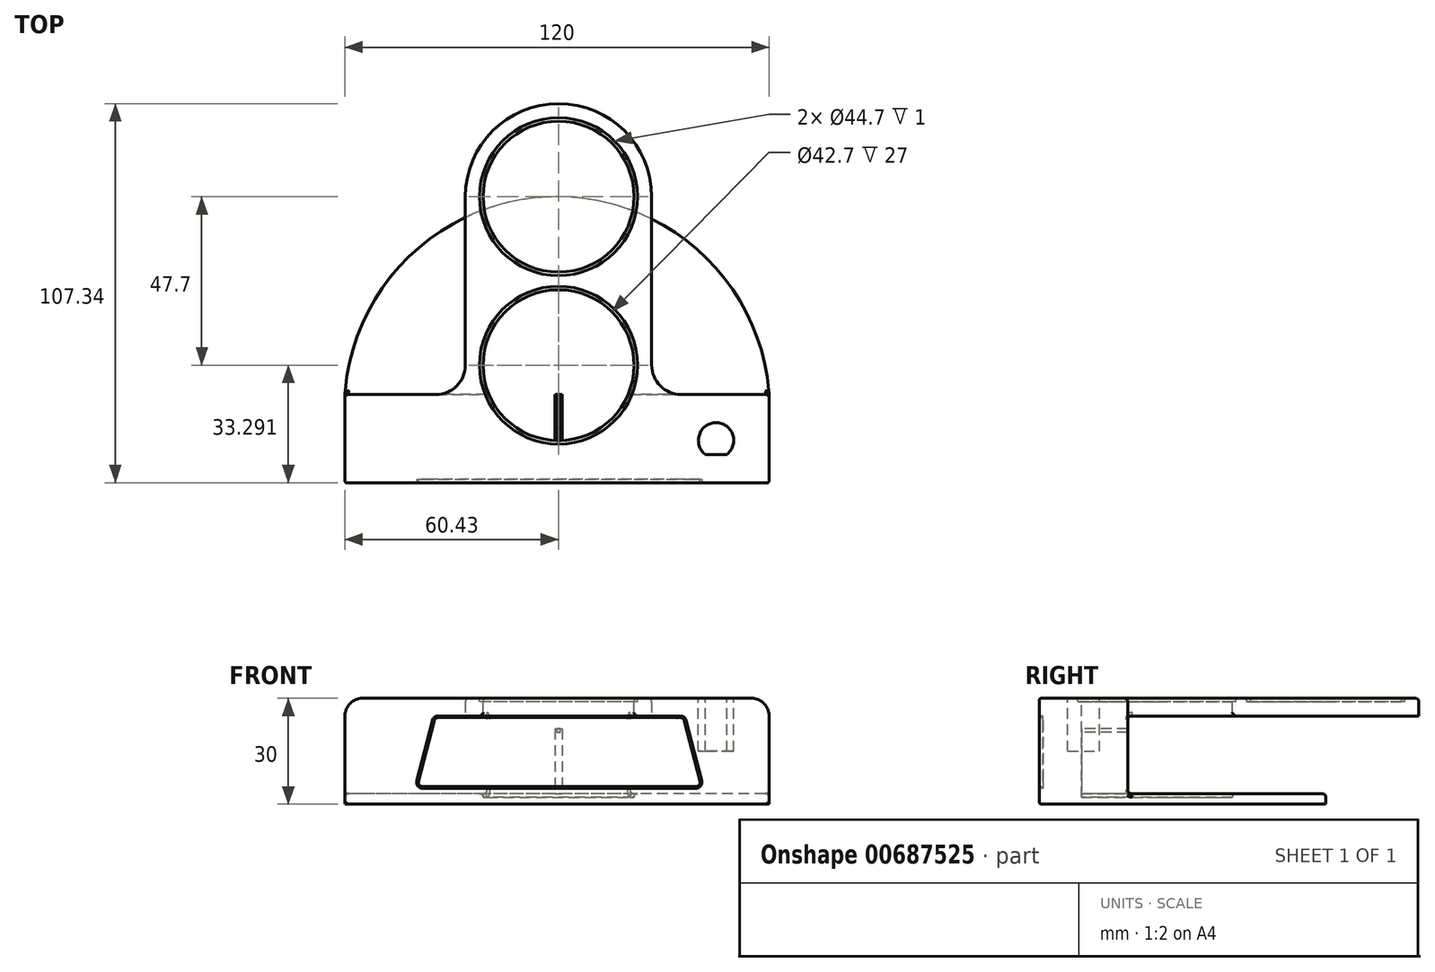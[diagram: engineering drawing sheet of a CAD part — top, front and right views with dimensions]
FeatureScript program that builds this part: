
annotation { "Feature Type Name" : "Feature", "Feature Type Description" : "" }
export const myFeature = defineFeature(function(context is Context, id is Id, definition is map)
    precondition{}
    {
        {
            var Q0;
            Q0=qCreatedBy(makeId("Top.planeOp"),FACE);
            var sketch = newSketch(context, id + "F0", { "sketchPlane" : qUnion([Q0])});
            skLineSegment(sketch, "E0", {"start": v(0, 0) * mm, "end": v(-60.43, 0) * mm, "construction": true});
            skLineSegment(sketch, "E1.bottom", {"start": v(-60.43, 0) * mm, "end": v(59.57, 0) * mm});
            skLineSegment(sketch, "E1.top", {"start": v(-60.43, 25) * mm, "end": v(59.57, 25) * mm});
            skLineSegment(sketch, "E1.left", {"start": v(-60.43, 0) * mm, "end": v(-60.43, 25) * mm});
            skLineSegment(sketch, "E1.right", {"start": v(59.57, 0) * mm, "end": v(59.57, 25) * mm});
            skSolve(sketch);
        }
        {
            var Q0;
            Q0=makeQuery(id+"F0.imprint","IMPRINT",FACE,{"disambiguationData":[TD([[makeQuery(id+"F0.imprint","IMPRINT",EDGE,{"derivedFrom":sQuery(id+"F0.wireOp",EDGE,"E1.bottom")}),1.0]])]});
            extrude(context, id + "F1", {"entities" : qUnion([Q0]), "depth" : 30 * mm, "offsetDistance" : 25 * mm});
        }
        {
            var Q0;
            Q0=qCreatedBy(makeId("Top.planeOp"),FACE);
            cPlane(context, id + "F2", {"entities" : qUnion([Q0]), "cplaneType" : CPlaneType.OFFSET, "offset" : 25 * mm, "width" : 150 * mm, "height" : 150 * mm});
        }
        {
            var Q0;
            Q0=qCreatedBy(id+"F2.planeOp",FACE);
            var sketch = newSketch(context, id + "F3", { "sketchPlane" : qUnion([Q0])});
            skCircle(sketch, "E2", {"center": v(0, 33.3) * mm, "radius": 21.35 * mm});
            skCircle(sketch, "E3", {"center": v(0, 81) * mm, "radius": 21.35 * mm});
            skLineSegment(sketch, "E4.0", {"start": v(-60.43, 25) * mm, "end": v(59.57, 25) * mm});
            skLineSegment(sketch, "E5.0.0", {"start": v(59.57, 25) * mm, "end": v(-60.43, 25) * mm});
            skLineSegment(sketch, "E5.0.1", {"start": v(-60.43, 25) * mm, "end": v(-60.43, 0) * mm});
            skLineSegment(sketch, "E5.0.2", {"start": v(-60.43, 0) * mm, "end": v(59.57, 0) * mm});
            skLineSegment(sketch, "E5.0.3", {"start": v(59.57, 0) * mm, "end": v(59.57, 25) * mm});
            skArc(sketch, "E6", {"start": v(-34.64, 25) * mm, "mid": v(-28.78, 27.43) * mm, "end": v(-26.35, 33.3) * mm});
            skArc(sketch, "E7.0", {"start": v(26.35, 81) * mm, "mid": v(0, 107.34) * mm, "end": v(-26.35, 81) * mm});
            skLineSegment(sketch, "E8", {"start": v(-26.35, 81) * mm, "end": v(-26.35, 33.3) * mm});
            skLineSegment(sketch, "E9", {"start": v(26.35, 81) * mm, "end": v(26.35, 33.3) * mm});
            skArc(sketch, "E10.MirrorC", {"start": v(34.64, 25) * mm, "mid": v(28.78, 27.43) * mm, "end": v(26.35, 33.3) * mm});
            skSolve(sketch);
        }
        {
            var Q0;
            Q0=makeQuery(id+"F3.imprint","IMPRINT",FACE,{"disambiguationData":[TD([[makeQuery(id+"F3.imprint","IMPRINT",EDGE,{"derivedFrom":sQuery(id+"F3.wireOp",EDGE,"E3")}),-1.0]])]});
            var Q1;
            {var subQ0=sQuery(id+"F3.wireOp",EDGE,"E5.0.0");var subQ1=sQuery(id+"F3.wireOp",EDGE,"E2");var subQ2=makeQuery(id+"F3.imprint","INTERSECT",VERTEX,{"disambiguationData":[OD(0.0)],"derivedFrom":[subQ1,subQ0]});Q1=makeQuery(id+"F3.imprint","IMPRINT",FACE,{"disambiguationData":[TD([[makeQuery(id+"F3.imprint","IMPRINT",EDGE,{"disambiguationData":[TD([[subQ2,-1.0]])],"derivedFrom":subQ1}),1.0]])]});}
            var Q2;
            Q2=makeQuery(id+"F3.imprint","IMPRINT",FACE,{"disambiguationData":[TD([[makeQuery(id+"F3.imprint","IMPRINT",EDGE,{"derivedFrom":sQuery(id+"F3.wireOp",EDGE,"E3")}),1.0]])]});
            extrude(context, id + "F4", {"entities" : qUnion([Q0, Q1, Q2]), "operationType" : NewBodyOperationType.ADD, "depth" : 5 * mm, "offsetDistance" : 25 * mm});
        }
        {
            var Q0;
            Q0=qCreatedBy(makeId("Top.planeOp"),FACE);
            var sketch = newSketch(context, id + "F5", { "sketchPlane" : qUnion([Q0])});
            skLineSegment(sketch, "E11.0", {"start": v(59.57, 25) * mm, "end": v(-60.43, 25) * mm});
            skPoint(sketch, "E12.0", {"position": v(0, 81) * mm});
            skArc(sketch, "E13", {"start": v(59.57, 25) * mm, "mid": v(-0.43, 81) * mm, "end": v(-60.43, 25) * mm});
            skLineSegment(sketch, "E14", {"start": v(-60.43, 25) * mm, "end": v(59.57, 25) * mm});
            skSolve(sketch);
        }
        {
            var Q0;
            Q0=makeQuery(id+"F5.imprint","IMPRINT",FACE,{"disambiguationData":[TD([[makeQuery(id+"F5.imprint","IMPRINT",EDGE,{"derivedFrom":sQuery(id+"F5.wireOp",EDGE,"E13")}),1.0]])]});
            extrude(context, id + "F6", {"entities" : qUnion([Q0]), "operationType" : NewBodyOperationType.ADD, "depth" : 3 * mm, "offsetDistance" : 25 * mm});
        }
        {
            var Q0;
            Q0=makeQuery(id+"F6.opExtrude","CAP_EDGE",EDGE,{"disambiguationData":[OSD([sQuery(id+"F5.wireOp",EDGE,"E13")])],"isStart":false});
            var Q1;
            Q1=makeQuery(id+"F1.opExtrude","SWEPT_FACE",FACE,{"disambiguationData":[OSD([sQuery(id+"F0.wireOp",EDGE,"E1.top")])]});
            fillet(context, id + "F7", {"entities" : qUnion([Q0, Q1]), "radius" : 1 * mm, "tangentPropagation" : true, "allowEdgeOverflow" : false});
        }
        {
            var Q0;
            Q0=makeQuery(id+"F4.boolean.opBoolean","MERGE",FACE,{"derivedFrom":[makeQuery(id+"F1.opExtrude","CAP_FACE",FACE,{"disambiguationData":[OSD([sQuery(id+"F0.wireOp",EDGE,"E1.bottom"),sQuery(id+"F0.wireOp",EDGE,"E1.top"),sQuery(id+"F0.wireOp",EDGE,"E1.left"),sQuery(id+"F0.wireOp",EDGE,"E1.right")])],"isStart":false}),makeQuery(id+"F4.opExtrude","CAP_FACE",FACE,{"disambiguationData":[OSD([sQuery(id+"F3.wireOp",EDGE,"E5.0.0"),sQuery(id+"F3.wireOp",EDGE,"E6"),sQuery(id+"F3.wireOp",EDGE,"E7.0"),sQuery(id+"F3.wireOp",EDGE,"E8"),sQuery(id+"F3.wireOp",EDGE,"E9"),sQuery(id+"F3.wireOp",EDGE,"E10.MirrorC")])],"isStart":false})]});
            var sketch = newSketch(context, id + "F8", { "sketchPlane" : qUnion([Q0])});
            skCircle(sketch, "E15.0", {"center": v(0, 81) * mm, "radius": 21.35 * mm});
            skCircle(sketch, "E16.0", {"center": v(0, 33.3) * mm, "radius": 21.35 * mm});
            skCircle(sketch, "E17.0", {"center": v(0, 81) * mm, "radius": 22.35 * mm});
            skCircle(sketch, "E18.0", {"center": v(0, 33.3) * mm, "radius": 22.35 * mm});
            skSolve(sketch);
        }
        {
            var Q0;
            Q0=makeQuery(id+"F8.imprint","IMPRINT",FACE,{"disambiguationData":[TD([[makeQuery(id+"F8.imprint","IMPRINT",EDGE,{"derivedFrom":sQuery(id+"F8.wireOp",EDGE,"E15.0")}),-1.0]])]});
            var Q1;
            Q1=makeQuery(id+"F8.imprint","IMPRINT",FACE,{"disambiguationData":[TD([[makeQuery(id+"F8.imprint","IMPRINT",EDGE,{"derivedFrom":sQuery(id+"F8.wireOp",EDGE,"E16.0")}),-1.0]])]});
            extrude(context, id + "F9", {"entities" : qUnion([Q0, Q1]), "operationType" : NewBodyOperationType.REMOVE, "oppositeDirection" : true, "depth" : 1 * mm, "offsetDistance" : 25 * mm});
        }
        {
            var Q0;
            Q0=makeQuery(id+"F9.boolean.opBoolean","SPLIT",FACE,{"disambiguationData":[TD([makeQuery(id+"F9.opExtrude","SWEPT_FACE",FACE,{"disambiguationData":[OSD([sQuery(id+"F8.wireOp",EDGE,"E15.0")])]})])],"derivedFrom":makeQuery(id+"F4.boolean.opBoolean","MERGE",FACE,{"derivedFrom":[makeQuery(id+"F1.opExtrude","CAP_FACE",FACE,{"disambiguationData":[OSD([sQuery(id+"F0.wireOp",EDGE,"E1.bottom"),sQuery(id+"F0.wireOp",EDGE,"E1.top"),sQuery(id+"F0.wireOp",EDGE,"E1.left"),sQuery(id+"F0.wireOp",EDGE,"E1.right")])],"isStart":false}),makeQuery(id+"F4.opExtrude","CAP_FACE",FACE,{"disambiguationData":[OSD([sQuery(id+"F3.wireOp",EDGE,"E5.0.0"),sQuery(id+"F3.wireOp",EDGE,"E6"),sQuery(id+"F3.wireOp",EDGE,"E7.0"),sQuery(id+"F3.wireOp",EDGE,"E8"),sQuery(id+"F3.wireOp",EDGE,"E9"),sQuery(id+"F3.wireOp",EDGE,"E10.MirrorC")])],"isStart":false})]})});
            extrude(context, id + "F10", {"entities" : qUnion([Q0]), "operationType" : NewBodyOperationType.REMOVE, "oppositeDirection" : true, "depth" : 1 * mm, "offsetDistance" : 25 * mm});
        }
        {
            var Q0;
            Q0=makeQuery(id+"F10.boolean.opBoolean","MERGE",FACE,{"derivedFrom":[makeQuery(id+"F9.boolean.opBoolean","COPY",FACE,{"derivedFrom":makeQuery(id+"F9.opExtrude","CAP_FACE",FACE,{"disambiguationData":[OSD([sQuery(id+"F8.wireOp",EDGE,"E15.0"),sQuery(id+"F8.wireOp",EDGE,"E17.0")])],"isStart":false})}),makeQuery(id+"F10.opExtrude","CAP_FACE",FACE,{"disambiguationData":[OSD([sQuery(id+"F0.wireOp",EDGE,"E1.bottom"),sQuery(id+"F0.wireOp",EDGE,"E1.top"),sQuery(id+"F0.wireOp",EDGE,"E1.left"),sQuery(id+"F0.wireOp",EDGE,"E1.right"),sQuery(id+"F3.wireOp",EDGE,"E5.0.0"),sQuery(id+"F3.wireOp",EDGE,"E6"),sQuery(id+"F3.wireOp",EDGE,"E7.0"),sQuery(id+"F3.wireOp",EDGE,"E8"),sQuery(id+"F3.wireOp",EDGE,"E9"),sQuery(id+"F3.wireOp",EDGE,"E10.MirrorC")])],"isStart":false})]});
            var sketch = newSketch(context, id + "F11", { "sketchPlane" : qUnion([Q0])});
            skCircle(sketch, "E19.0", {"center": v(0, 81) * mm, "radius": 21.35 * mm});
            skSolve(sketch);
        }
        {
            var Q0;
            Q0=makeQuery(id+"F11.imprint","IMPRINT",FACE,{"disambiguationData":[TD([[makeQuery(id+"F11.imprint","IMPRINT",EDGE,{"derivedFrom":sQuery(id+"F11.wireOp",EDGE,"E19.0")}),1.0]])]});
            extrude(context, id + "F12", {"entities" : qUnion([Q0]), "depth" : 1 * mm, "offsetDistance" : 25 * mm});
        }
        {
            var Q0;
            Q0=makeQuery(id+"F9.boolean.opBoolean","SPLIT",FACE,{"disambiguationData":[TD([makeQuery(id+"F9.opExtrude","SWEPT_FACE",FACE,{"disambiguationData":[OSD([sQuery(id+"F8.wireOp",EDGE,"E16.0")])]})])],"derivedFrom":makeQuery(id+"F4.boolean.opBoolean","MERGE",FACE,{"derivedFrom":[makeQuery(id+"F1.opExtrude","CAP_FACE",FACE,{"disambiguationData":[OSD([sQuery(id+"F0.wireOp",EDGE,"E1.bottom"),sQuery(id+"F0.wireOp",EDGE,"E1.top"),sQuery(id+"F0.wireOp",EDGE,"E1.left"),sQuery(id+"F0.wireOp",EDGE,"E1.right")])],"isStart":false}),makeQuery(id+"F4.opExtrude","CAP_FACE",FACE,{"disambiguationData":[OSD([sQuery(id+"F3.wireOp",EDGE,"E5.0.0"),sQuery(id+"F3.wireOp",EDGE,"E6"),sQuery(id+"F3.wireOp",EDGE,"E7.0"),sQuery(id+"F3.wireOp",EDGE,"E8"),sQuery(id+"F3.wireOp",EDGE,"E9"),sQuery(id+"F3.wireOp",EDGE,"E10.MirrorC")])],"isStart":false})]})});
            var Q1;
            Q1=makeQuery(id+"F6.opExtrude","CAP_FACE",FACE,{"disambiguationData":[OSD([sQuery(id+"F5.wireOp",EDGE,"E13"),sQuery(id+"F5.wireOp",EDGE,"E14")])],"isStart":false});
            extrude(context, id + "F13", {"entities" : qUnion([Q0]), "operationType" : NewBodyOperationType.REMOVE, "endBound" : BoundingType.UP_TO_SURFACE, "oppositeDirection" : true, "depth" : 25 * mm, "endBoundEntityFace" : qUnion([Q1]), "offsetDistance" : 25 * mm});
        }
        {
            var Q0;
            {var subQ0=sQuery(id+"F5.wireOp",EDGE,"E14");var subQ1=sQuery(id+"F5.wireOp",EDGE,"E13");Q0=makeQuery(id+"F13.boolean.opBoolean","MERGE",FACE,{"derivedFrom":[makeQuery(id+"F6.opExtrude","CAP_FACE",FACE,{"disambiguationData":[OSD([subQ1,subQ0])],"isStart":false}),makeQuery(id+"F13.opExtrude","CAP_FACE",FACE,{"disambiguationData":[OSD([subQ1,subQ0])],"isStart":false})]});}
            var sketch = newSketch(context, id + "F14", { "sketchPlane" : qUnion([Q0])});
            skArc(sketch, "E20.0.0", {"start": v(19.67, 25) * mm, "mid": v(0, 54.64) * mm, "end": v(-19.67, 25) * mm});
            skArc(sketch, "E21.0.1", {"start": v(-19.67, 25) * mm, "mid": v(0, 11.94) * mm, "end": v(19.67, 25) * mm});
            skSolve(sketch);
        }
        {
            var Q0;
            Q0 = qSketchRegion(id + "F14", true);
            extrude(context, id + "F15", {"entities" : qUnion([Q0]), "operationType" : NewBodyOperationType.REMOVE, "oppositeDirection" : true, "depth" : 1 * mm, "offsetDistance" : 25 * mm});
        }
        {
            var Q0;
            Q0=makeQuery(id+"F15.boolean.opBoolean","COPY",FACE,{"derivedFrom":makeQuery(id+"F15.opExtrude","CAP_FACE",FACE,{"disambiguationData":[OSD([sQuery(id+"F14.wireOp",EDGE,"E20.0.0"),sQuery(id+"F14.wireOp",EDGE,"E21.0.1")])],"isStart":false})});
            var sketch = newSketch(context, id + "F16", { "sketchPlane" : qUnion([Q0])});
            skCircle(sketch, "E22.0.0", {"center": v(0, 33.3) * mm, "radius": 21.35 * mm});
            skSolve(sketch);
        }
        {
            var Q0;
            Q0 = qSketchRegion(id + "F16", true);
            extrude(context, id + "F17", {"entities" : qUnion([Q0]), "depth" : 1 * mm, "offsetDistance" : 25 * mm});
        }
        {
            var Q0;
            Q0=makeQuery(id+"F17.opExtrude","CAP_FACE",FACE,{"disambiguationData":[OSD([sQuery(id+"F16.wireOp",EDGE,"E22.0.0")])],"isStart":false});
            var sketch = newSketch(context, id + "F18", { "sketchPlane" : qUnion([Q0])});
            skArc(sketch, "E23.0.0", {"start": v(19.67, 25) * mm, "mid": v(0, 54.64) * mm, "end": v(-19.67, 25) * mm});
            skLineSegment(sketch, "E23.0.1", {"start": v(-19.67, 25) * mm, "end": v(19.67, 25) * mm});
            skPoint(sketch, "E24.end.orphan", {"position": v(0, 25) * mm});
            skLineSegment(sketch, "E25.0.0", {"start": v(19.67, 25) * mm, "end": v(-19.67, 25) * mm});
            skArc(sketch, "E25.0.1", {"start": v(-19.67, 25) * mm, "mid": v(0, 11.94) * mm, "end": v(19.67, 25) * mm});
            skLineSegment(sketch, "E26", {"start": v(0, 11.94) * mm, "end": v(0, 25) * mm});
            skLineSegment(sketch, "E27", {"start": v(0, 25) * mm, "end": v(-1, 25) * mm});
            skLineSegment(sketch, "E28.bottom", {"start": v(-1, 25) * mm, "end": v(1, 25) * mm});
            skLineSegment(sketch, "E29", {"start": v(-1, 25) * mm, "end": v(-1, 11.96) * mm});
            skLineSegment(sketch, "E30", {"start": v(1, 11.96) * mm, "end": v(1, 25) * mm});
            skSolve(sketch);
        }
        {
            var Q0;
            {var subQ0=sQuery(id+"F18.wireOp",EDGE,"E26");Q0=makeQuery(id+"F18.imprint","IMPRINT",FACE,{"disambiguationData":[TD([[makeQuery(id+"F18.imprint","IMPRINT",EDGE,{"derivedFrom":subQ0}),1.0]])]});}
            var Q1;
            {var subQ0=sQuery(id+"F18.wireOp",EDGE,"E26");Q1=makeQuery(id+"F18.imprint","IMPRINT",FACE,{"disambiguationData":[TD([[makeQuery(id+"F18.imprint","IMPRINT",EDGE,{"derivedFrom":subQ0}),-1.0]])]});}
            extrude(context, id + "F19", {"entities" : qUnion([Q0, Q1]), "depth" : (21.35 - 3) * mm, "offsetDistance" : 25 * mm});
        }
        {
            var Q0;
            Q0=makeQuery(id+"F19.opExtrude","CAP_FACE",FACE,{"disambiguationData":[OSD([sQuery(id+"F18.wireOp",EDGE,"E25.0.1"),sQuery(id+"F18.wireOp",EDGE,"E29"),sQuery(id+"F18.wireOp",EDGE,"E30"),sQuery(id+"F18.wireOp",EDGE,"E28.bottom")])],"isStart":false});
            var sketch = newSketch(context, id + "F20", { "sketchPlane" : qUnion([Q0])});
            skLineSegment(sketch, "E31", {"start": v(0, 25) * mm, "end": v(-0.5, 25) * mm});
            skLineSegment(sketch, "E32", {"start": v(0, 11.94) * mm, "end": v(0.5, 11.95) * mm});
            skLineSegment(sketch, "E33.bottom", {"start": v(-0.5, 25) * mm, "end": v(0.5, 25) * mm});
            skLineSegment(sketch, "E33.top", {"start": v(-0.5, 11.95) * mm, "end": v(0.5, 11.95) * mm});
            skLineSegment(sketch, "E33.left", {"start": v(-0.5, 25) * mm, "end": v(-0.5, 11.95) * mm});
            skLineSegment(sketch, "E33.right", {"start": v(0.5, 25) * mm, "end": v(0.5, 11.95) * mm});
            skSolve(sketch);
        }
        {
            var Q0;
            Q0=makeQuery(id+"F20.imprint","IMPRINT",FACE,{"disambiguationData":[TD([[makeQuery(id+"F20.imprint","IMPRINT",EDGE,{"derivedFrom":sQuery(id+"F20.wireOp",EDGE,"E33.top")}),1.0]])]});
            extrude(context, id + "F21", {"entities" : qUnion([Q0]), "operationType" : NewBodyOperationType.REMOVE, "oppositeDirection" : true, "depth" : 1 * mm, "offsetDistance" : 25 * mm});
        }
        {
            var Q0;
            Q0=makeQuery(id+"F21.boolean.opBoolean","COPY",FACE,{"derivedFrom":makeQuery(id+"F21.opExtrude","CAP_FACE",FACE,{"disambiguationData":[OSD([sQuery(id+"F20.wireOp",EDGE,"E33.bottom"),sQuery(id+"F20.wireOp",EDGE,"E33.top"),sQuery(id+"F20.wireOp",EDGE,"E33.left"),sQuery(id+"F20.wireOp",EDGE,"E33.right")])],"isStart":false})});
            var sketch = newSketch(context, id + "F22", { "sketchPlane" : qUnion([Q0])});
            skLineSegment(sketch, "E34.0.0", {"start": v(0.5, 11.95) * mm, "end": v(0.5, 25) * mm});
            skLineSegment(sketch, "E34.0.1", {"start": v(0.5, 25) * mm, "end": v(-0.5, 25) * mm});
            skLineSegment(sketch, "E34.0.2", {"start": v(-0.5, 25) * mm, "end": v(-0.5, 11.95) * mm});
            skArc(sketch, "E34.0.3", {"start": v(-0.5, 11.95) * mm, "mid": v(0, 11.94) * mm, "end": v(0.5, 11.95) * mm});
            skSolve(sketch);
        }
        {
            var Q0;
            Q0=makeQuery(id+"F22.imprint","IMPRINT",FACE,{"disambiguationData":[TD([[makeQuery(id+"F22.imprint","IMPRINT",EDGE,{"derivedFrom":sQuery(id+"F22.wireOp",EDGE,"E34.0.0")}),-1.0]])]});
            extrude(context, id + "F23", {"entities" : qUnion([Q0]), "depth" : 1 * mm, "offsetDistance" : 25 * mm});
        }
        {
            var Q0;
            {var subQ0=sQuery(id+"F3.wireOp",EDGE,"E10.MirrorC");var subQ1=sQuery(id+"F3.wireOp",EDGE,"E9");var subQ2=sQuery(id+"F3.wireOp",EDGE,"E8");var subQ3=sQuery(id+"F3.wireOp",EDGE,"E7.0");var subQ4=sQuery(id+"F3.wireOp",EDGE,"E6");var subQ5=makeQuery(id+"F4.opExtrude","CAP_FACE",FACE,{"disambiguationData":[OSD([sQuery(id+"F3.wireOp",EDGE,"E5.0.0"),subQ4,subQ3,subQ2,subQ1,subQ0])],"isStart":false});var subQ6=sQuery(id+"F0.wireOp",EDGE,"E1.right");var subQ8=sQuery(id+"F0.wireOp",EDGE,"E1.top");var subQ10=sQuery(id+"F0.wireOp",EDGE,"E1.left");var subQ11=sQuery(id+"F0.wireOp",EDGE,"E1.bottom");var subQ12=makeQuery(id+"F1.opExtrude","CAP_FACE",FACE,{"disambiguationData":[OSD([subQ11,subQ8,subQ10,subQ6])],"isStart":false});Q0=makeQuery(id+"F9.boolean.opBoolean","SPLIT",FACE,{"disambiguationData":[TD([makeQuery(id+"F1.opExtrude","SWEPT_FACE",FACE,{"disambiguationData":[OSD([subQ11])]})])],"derivedFrom":makeQuery(id+"F4.boolean.opBoolean","MERGE",FACE,{"derivedFrom":[subQ12,subQ5]})});}
            var sketch = newSketch(context, id + "F24", { "sketchPlane" : qUnion([Q0])});
            skLineSegment(sketch, "E35", {"start": v(59.57, 12) * mm, "end": v(44.57, 12) * mm});
            skArc(sketch, "E36", {"start": v(47.59, 8.02) * mm, "mid": v(44.57, 17) * mm, "end": v(41.54, 8.02) * mm});
            skLineSegment(sketch, "E37", {"start": v(41.54, 8.02) * mm, "end": v(47.59, 8.02) * mm});
            skSolve(sketch);
        }
        {
            var Q0;
            {var subQ0=sQuery(id+"F24.wireOp",EDGE,"E37");Q0=makeQuery(id+"F24.imprint","IMPRINT",FACE,{"disambiguationData":[TD([[makeQuery(id+"F24.imprint","IMPRINT",EDGE,{"derivedFrom":subQ0}),1.0]])]});}
            extrude(context, id + "F25", {"entities" : qUnion([Q0]), "operationType" : NewBodyOperationType.REMOVE, "oppositeDirection" : true, "depth" : 15 * mm, "offsetDistance" : 25 * mm});
        }
        {
            var Q0;
            Q0=makeQuery(id+"F1.opExtrude","CAP_EDGE",EDGE,{"disambiguationData":[OSD([sQuery(id+"F0.wireOp",EDGE,"E1.bottom")])],"isStart":false});
            var Q1;
            Q1=makeQuery(id+"F1.opExtrude","SWEPT_FACE",FACE,{"disambiguationData":[OSD([sQuery(id+"F0.wireOp",EDGE,"E1.bottom")])]});
            fillet(context, id + "F26", {"entities" : qUnion([Q0, Q1]), "radius" : 0.5 * mm, "tangentPropagation" : true, "allowEdgeOverflow" : false});
        }
        {
            var Q0;
            Q0=makeQuery(id+"F1.opExtrude","SWEPT_FACE",FACE,{"disambiguationData":[OSD([sQuery(id+"F0.wireOp",EDGE,"E1.bottom")])]});
            var sketch = newSketch(context, id + "F27", { "sketchPlane" : qUnion([Q0])});
            skLineSegment(sketch, "E38", {"start": v(0, 0) * mm, "end": v(0, 5) * mm});
            skLineSegment(sketch, "E39", {"start": v(0, 29.5) * mm, "end": v(0, 24.5) * mm});
            skLineSegment(sketch, "E40", {"start": v(0, 24.5) * mm, "end": v(-34.08, 24.5) * mm});
            skLineSegment(sketch, "E41.bottom", {"start": v(-34.08, 24.5) * mm, "end": v(34.46, 24.5) * mm});
            skLineSegment(sketch, "E41.top", {"start": v(-35, 5) * mm, "end": v(35.38, 5) * mm});
            skLineSegment(sketch, "E42", {"start": v(-35, 5) * mm, "end": v(-38.47, 5) * mm});
            skLineSegment(sketch, "E43", {"start": v(35.38, 5) * mm, "end": v(38.85, 5) * mm});
            skLineSegment(sketch, "E44", {"start": v(-35.23, 23.6) * mm, "end": v(-39.62, 6.48) * mm});
            skLineSegment(sketch, "E45", {"start": v(35.61, 23.6) * mm, "end": v(40, 6.48) * mm});
            skArc(sketch, "E46.filletArc", {"start": v(-34.08, 24.5) * mm, "mid": v(-34.8, 24.25) * mm, "end": v(-35.23, 23.6) * mm});
            skPoint(sketch, "E47.visualSharp", {"position": v(-40, 5) * mm});
            skArc(sketch, "E47.filletArc", {"start": v(-39.62, 6.48) * mm, "mid": v(-39.4, 5.46) * mm, "end": v(-38.47, 5) * mm});
            skPoint(sketch, "E48.visualSharp", {"position": v(40.38, 5) * mm});
            skArc(sketch, "E48.filletArc", {"start": v(38.85, 5) * mm, "mid": v(39.8, 5.46) * mm, "end": v(40, 6.48) * mm});
            skArc(sketch, "E49.filletArc", {"start": v(35.61, 23.6) * mm, "mid": v(35.2, 24.25) * mm, "end": v(34.46, 24.5) * mm});
            skLineSegment(sketch, "E50.0", {"start": v(-34.08, 25) * mm, "end": v(34.46, 25) * mm});
            skArc(sketch, "E50.1", {"start": v(36.1, 23.73) * mm, "mid": v(35.5, 24.65) * mm, "end": v(34.46, 25) * mm});
            skArc(sketch, "E50.2", {"start": v(-34.08, 25) * mm, "mid": v(-35.11, 24.65) * mm, "end": v(-35.71, 23.73) * mm});
            skLineSegment(sketch, "E50.3", {"start": v(36.1, 23.73) * mm, "end": v(40.49, 6.6) * mm});
            skArc(sketch, "E50.4", {"start": v(38.85, 4.5) * mm, "mid": v(40.19, 5.15) * mm, "end": v(40.49, 6.6) * mm});
            skLineSegment(sketch, "E50.5", {"start": v(35.38, 4.5) * mm, "end": v(38.85, 4.5) * mm});
            skLineSegment(sketch, "E50.6", {"start": v(-35.71, 23.73) * mm, "end": v(-40.1, 6.6) * mm});
            skArc(sketch, "E50.7", {"start": v(-40.1, 6.6) * mm, "mid": v(-39.8, 5.15) * mm, "end": v(-38.47, 4.5) * mm});
            skLineSegment(sketch, "E50.8", {"start": v(-35, 4.5) * mm, "end": v(-38.47, 4.5) * mm});
            skLineSegment(sketch, "E50.9", {"start": v(-35, 4.5) * mm, "end": v(35.38, 4.5) * mm});
            skSolve(sketch);
        }
        {
            var Q0;
            {var subQ4=sQuery(id+"F27.wireOp",EDGE,"E42");Q0=makeQuery(id+"F27.imprint","IMPRINT",FACE,{"disambiguationData":[TD([[makeQuery(id+"F27.imprint","IMPRINT",EDGE,{"derivedFrom":subQ4}),1.0]])]});}
            var Q1;
            {var subQ5=sQuery(id+"F27.wireOp",EDGE,"E43");Q1=makeQuery(id+"F27.imprint","IMPRINT",FACE,{"disambiguationData":[TD([[makeQuery(id+"F27.imprint","IMPRINT",EDGE,{"derivedFrom":subQ5}),-1.0]])]});}
            extrude(context, id + "F28", {"entities" : qUnion([Q0, Q1]), "operationType" : NewBodyOperationType.REMOVE, "oppositeDirection" : true, "depth" : 1 * mm, "offsetDistance" : 25 * mm});
        }
        {
            var Q0;
            Q0=makeQuery(id+"F28.boolean.opBoolean","SPLIT",FACE,{"disambiguationData":[TD([makeQuery(id+"F28.opExtrude","SWEPT_FACE",FACE,{"disambiguationData":[OSD([sQuery(id+"F27.wireOp",EDGE,"E41.bottom")])]})])],"derivedFrom":makeQuery(id+"F1.opExtrude","SWEPT_FACE",FACE,{"disambiguationData":[OSD([sQuery(id+"F0.wireOp",EDGE,"E1.bottom")])]})});
            extrude(context, id + "F29", {"entities" : qUnion([Q0]), "operationType" : NewBodyOperationType.REMOVE, "oppositeDirection" : true, "depth" : 1 * mm, "offsetDistance" : 25 * mm});
        }
        {
            var Q0;
            Q0=makeQuery(id+"F29.boolean.opBoolean","MERGE",FACE,{"derivedFrom":[makeQuery(id+"F28.boolean.opBoolean","COPY",FACE,{"derivedFrom":makeQuery(id+"F28.opExtrude","CAP_FACE",FACE,{"disambiguationData":[OSD([sQuery(id+"F27.wireOp",EDGE,"E41.bottom"),sQuery(id+"F27.wireOp",EDGE,"E41.top"),sQuery(id+"F27.wireOp",EDGE,"E42"),sQuery(id+"F27.wireOp",EDGE,"E43"),sQuery(id+"F27.wireOp",EDGE,"E44"),sQuery(id+"F27.wireOp",EDGE,"E45"),sQuery(id+"F27.wireOp",EDGE,"E46.filletArc"),sQuery(id+"F27.wireOp",EDGE,"E47.filletArc"),sQuery(id+"F27.wireOp",EDGE,"E48.filletArc"),sQuery(id+"F27.wireOp",EDGE,"E49.filletArc"),sQuery(id+"F27.wireOp",EDGE,"E50.0"),sQuery(id+"F27.wireOp",EDGE,"E50.1"),sQuery(id+"F27.wireOp",EDGE,"E50.2"),sQuery(id+"F27.wireOp",EDGE,"E50.3"),sQuery(id+"F27.wireOp",EDGE,"E50.4"),sQuery(id+"F27.wireOp",EDGE,"E50.5"),sQuery(id+"F27.wireOp",EDGE,"E50.6"),sQuery(id+"F27.wireOp",EDGE,"E50.7"),sQuery(id+"F27.wireOp",EDGE,"E50.8"),sQuery(id+"F27.wireOp",EDGE,"E50.9")])],"isStart":false})}),makeQuery(id+"F29.opExtrude","CAP_FACE",FACE,{"disambiguationData":[OSD([sQuery(id+"F0.wireOp",EDGE,"E1.bottom")])],"isStart":false})]});
            var sketch = newSketch(context, id + "F30", { "sketchPlane" : qUnion([Q0])});
            skLineSegment(sketch, "E51.0.0", {"start": v(-38.47, 5) * mm, "end": v(-35, 5) * mm});
            skLineSegment(sketch, "E51.0.1", {"start": v(-35, 5) * mm, "end": v(0, 5) * mm});
            skLineSegment(sketch, "E51.0.2", {"start": v(0, 5) * mm, "end": v(35.38, 5) * mm});
            skLineSegment(sketch, "E51.0.3", {"start": v(35.38, 5) * mm, "end": v(38.85, 5) * mm});
            skArc(sketch, "E51.0.4", {"start": v(38.85, 5) * mm, "mid": v(39.8, 5.46) * mm, "end": v(40, 6.48) * mm});
            skLineSegment(sketch, "E51.0.5", {"start": v(40, 6.48) * mm, "end": v(35.61, 23.6) * mm});
            skArc(sketch, "E51.0.6", {"start": v(35.61, 23.6) * mm, "mid": v(35.2, 24.25) * mm, "end": v(34.46, 24.5) * mm});
            skLineSegment(sketch, "E51.0.7", {"start": v(34.46, 24.5) * mm, "end": v(0, 24.5) * mm});
            skLineSegment(sketch, "E51.0.8", {"start": v(0, 24.5) * mm, "end": v(-34.08, 24.5) * mm});
            skArc(sketch, "E51.0.9", {"start": v(-34.08, 24.5) * mm, "mid": v(-34.8, 24.25) * mm, "end": v(-35.23, 23.6) * mm});
            skLineSegment(sketch, "E51.0.10", {"start": v(-35.23, 23.6) * mm, "end": v(-39.62, 6.48) * mm});
            skArc(sketch, "E51.0.11", {"start": v(-39.62, 6.48) * mm, "mid": v(-39.4, 5.46) * mm, "end": v(-38.47, 5) * mm});
            skSolve(sketch);
        }
        {
            var Q0;
            Q0=makeQuery(id+"F30.imprint","IMPRINT",FACE,{"disambiguationData":[TD([[makeQuery(id+"F30.imprint","IMPRINT",EDGE,{"derivedFrom":sQuery(id+"F30.wireOp",EDGE,"E51.0.0")}),1.0]])]});
            extrude(context, id + "F31", {"entities" : qUnion([Q0]), "depth" : 1 * mm, "offsetDistance" : 25 * mm});
        }
        {
            var Q0;
            Q0=makeQuery(id+"F1.opExtrude","CAP_EDGE",EDGE,{"disambiguationData":[OSD([sQuery(id+"F0.wireOp",EDGE,"E1.left")])],"isStart":false});
            var Q1;
            Q1=makeQuery(id+"F1.opExtrude","CAP_EDGE",EDGE,{"disambiguationData":[OSD([sQuery(id+"F0.wireOp",EDGE,"E1.right")])],"isStart":false});
            fillet(context, id + "F32", {"entities" : qUnion([Q0, Q1]), "radius" : 5 * mm, "tangentPropagation" : true, "allowEdgeOverflow" : false});
        }
        {
            var Q0;
            Q0=makeQuery(id+"F13.boolean.opBoolean","INTERSECT",EDGE,{"disambiguationData":[OD(0.0)],"derivedFrom":[makeQuery(id+"F1.opExtrude","SWEPT_FACE",FACE,{"disambiguationData":[OSD([sQuery(id+"F0.wireOp",EDGE,"E1.top")])]}),makeQuery(id+"F13.opExtrude","SWEPT_FACE",FACE,{"disambiguationData":[OSD([sQuery(id+"F8.wireOp",EDGE,"E16.0")])]})]});
            fillet(context, id + "F33", {"entities" : qUnion([Q0]), "radius" : 1 * mm, "tangentPropagation" : true, "allowEdgeOverflow" : false});
        }
    });
